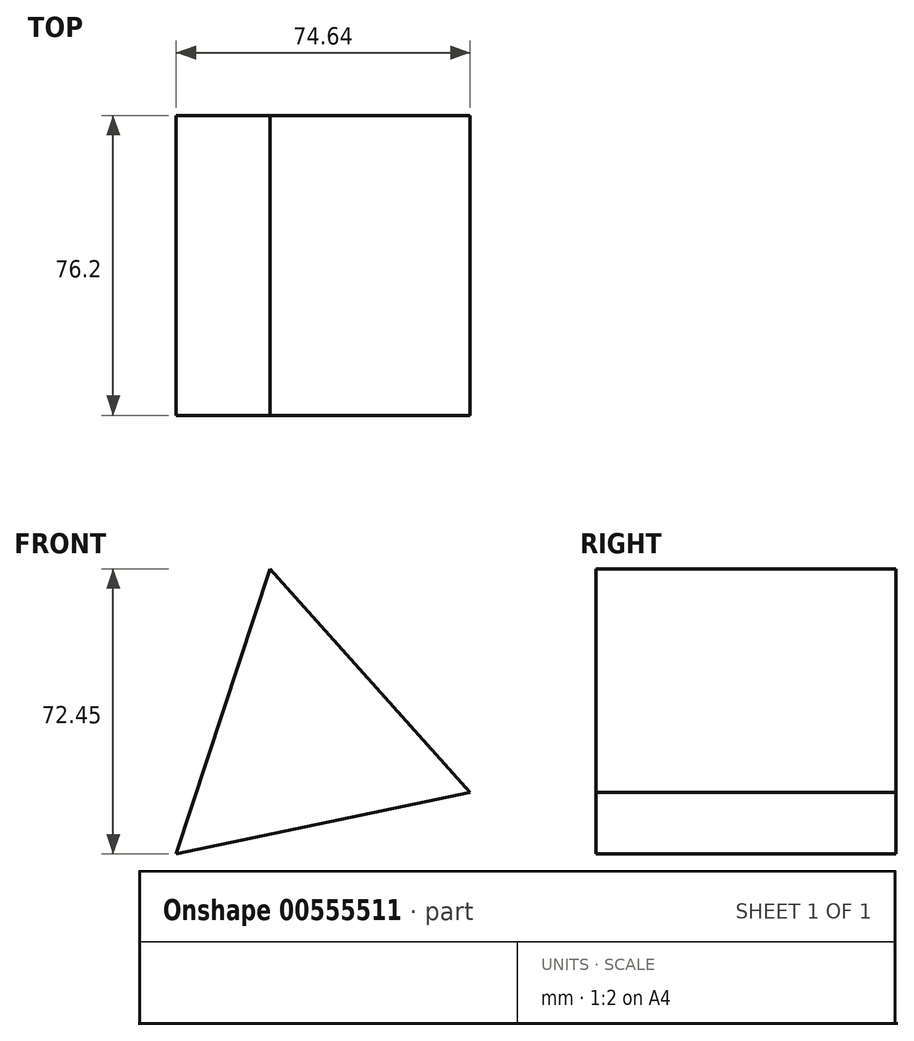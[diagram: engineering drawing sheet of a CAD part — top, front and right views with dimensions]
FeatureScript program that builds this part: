
annotation { "Feature Type Name" : "Feature", "Feature Type Description" : "" }
export const myFeature = defineFeature(function(context is Context, id is Id, definition is map)
    precondition{}
    {
        {
            var Q0;
            Q0=qCreatedBy(makeId("Front.planeOp"),FACE);
            var sketch = newSketch(context, id + "F0", { "sketchPlane" : qUnion([Q0])});
            skCircle(sketch, "E0.cCircle", {"center": v(0, 0) * mm, "radius": 22.01 * mm, "construction": true});
            skLineSegment(sketch, "E0.0", {"start": v(-9.02, 43.1) * mm, "end": v(41.83, -13.74) * mm});
            skLineSegment(sketch, "E0.1", {"start": v(41.83, -13.74) * mm, "end": v(-32.8, -29.36) * mm});
            skLineSegment(sketch, "E0.2", {"start": v(-32.8, -29.36) * mm, "end": v(-9.02, 43.1) * mm});
            skPoint(sketch, "E0.0.midPoint", {"position": v(16.4, 14.68) * mm});
            skSolve(sketch);
        }
        {
            var Q0;
            Q0=makeQuery(id+"F0.imprint","IMPRINT",FACE,{"disambiguationData":[TD([[makeQuery(id+"F0.imprint","IMPRINT",EDGE,{"derivedFrom":sQuery(id+"F0.wireOp",EDGE,"E0.0")}),-1.0]])]});
            extrude(context, id + "F1", {"entities" : qUnion([Q0]), "depth" : 76.2 * mm, "offsetDistance" : 25.4 * mm});
        }
    });
